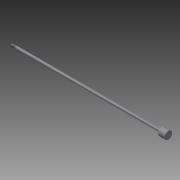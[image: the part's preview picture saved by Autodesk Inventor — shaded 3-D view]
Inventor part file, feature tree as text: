
AUTODESK INVENTOR PART (.ipt)
format: ipt  version: 2014 SP2 (Build 180246200, 246)  size: 151,040 bytes
history: native  units: in
note: dims shown in document units (in); Inventor stores cm internally (conversion verified against a paired STEP export)
features: other x112, sketch x3, revolve x2, thread x1, extrude x1
ambient origin geometry x8: Origin, YZ Plane, XZ Plane, XY Plane, X Axis, Y Axis, Z Axis, Center Point
bodies: Solid1 (feature_tree)
feature tree (119):
  revolve  "Revolution1"  Angle=360.0deg
  revolve  "Revolution2"  [1 undecoded]
  thread  "Thread1"  [1 undecoded]
  extrude  "Extrusion1"  [1 undecoded]
  other  "dia1_XY"
  other  "dia1_YZ"
  other  "dia1_ZX"
  other  "dia1_X"
  other  "dia1_Y"
  other  "dia1_Z"
  other  "dia1_Center"
  other  "dia12_XY"
  other  "dia12_YZ"
  other  "dia12_ZX"
  other  "dia12_X"
  other  "dia12_Y"
  other  "dia12_Z"
  other  "dia12_Center"
  other  "dia2_XY"
  other  "dia2_YZ"
  other  "dia2_ZX"
  other  "dia2_X"
  other  "dia2_Y"
  other  "dia2_Z"
  other  "dia2_Center"
  other  "dia22_XY"
  other  "dia22_YZ"
  other  "dia22_ZX"
  other  "dia22_X"
  other  "dia22_Y"
  other  "dia22_Z"
  other  "dia22_Center"
  other  "hh1_XY"
  other  "hh1_YZ"
  other  "hh1_ZX"
  other  "hh1_X"
  other  "hh1_Y"
  other  "hh1_Z"
  other  "hh1_Center"
  other  "hh2_XY"
  other  "hh2_YZ"
  other  "hh2_ZX"
  other  "hh2_X"
  other  "hh2_Y"
  other  "hh2_Z"
  other  "hh2_Center"
  other  "rl1_XY"
  other  "rl1_YZ"
  other  "rl1_ZX"
  other  "rl1_X"
  other  "rl1_Y"
  other  "rl1_Z"
  other  "rl1_Center"
  other  "rl2_XY"
  other  "rl2_YZ"
  other  "rl2_ZX"
  other  "rl2_X"
  other  "rl2_Y"
  other  "rl2_Z"
  other  "rl2_Center"
  other  "rod_cp_XY"
  other  "rod_cp_YZ"
  other  "rod_cp_ZX"
  other  "rod_cp_X"
  other  "rod_cp_Y"
  other  "rod_cp_Z"
  other  "rod_cp_Center"
  other  "thd1_XY"
  other  "thd1_YZ"
  other  "thd1_ZX"
  other  "thd1_X"
  other  "thd1_Y"
  other  "thd1_Z"
  other  "thd1_Center"
  other  "thd2_XY"
  other  "thd2_YZ"
  other  "thd2_ZX"
  other  "thd2_X"
  other  "thd2_Y"
  other  "thd2_Z"
  other  "thd2_Center"
  other  "to_rod_clevis_XY"
  other  "to_rod_clevis_YZ"
  other  "to_rod_clevis_ZX"
  other  "to_rod_clevis_X"
  other  "to_rod_clevis_Y"
  other  "to_rod_clevis_Z"
  other  "to_rod_clevis_Center"
  other  "wf1_XY"
  other  "wf1_YZ"
  other  "wf1_ZX"
  other  "wf1_X"
  other  "wf1_Y"
  other  "wf1_Z"
  other  "wf1_Center"
  other  "wf2_XY"
  other  "wf2_YZ"
  other  "wf2_ZX"
  other  "wf2_X"
  other  "wf2_Y"
  other  "wf2_Z"
  other  "wf2_Center"
  other  "wfw1_XY"
  other  "wfw1_YZ"
  other  "wfw1_ZX"
  other  "wfw1_X"
  other  "wfw1_Y"
  other  "wfw1_Z"
  other  "wfw1_Center"
  other  "wfw2_XY"
  other  "wfw2_YZ"
  other  "wfw2_ZX"
  other  "wfw2_X"
  other  "wfw2_Y"
  other  "wfw2_Z"
  other  "wfw2_Center"
  sketch  "Sketch_1"  dims[d0=360.0deg d1=360.0deg]
  sketch  "Sketch_3"  dims[d2=0.7203in d3=0.0in d4=0.25in d5=0.0in]
  sketch  "Sketch_10"  dims[d6=0.0in d7=0.0in d8=0.0in d9=0.0in d10=0.0in d11=0.0in d12=0.0in]
note: 3 required parameter values undecoded (feature->parameter linkage not recoverable at this tier; creation-order binding heuristic only, values carry confidence <= 0.55)